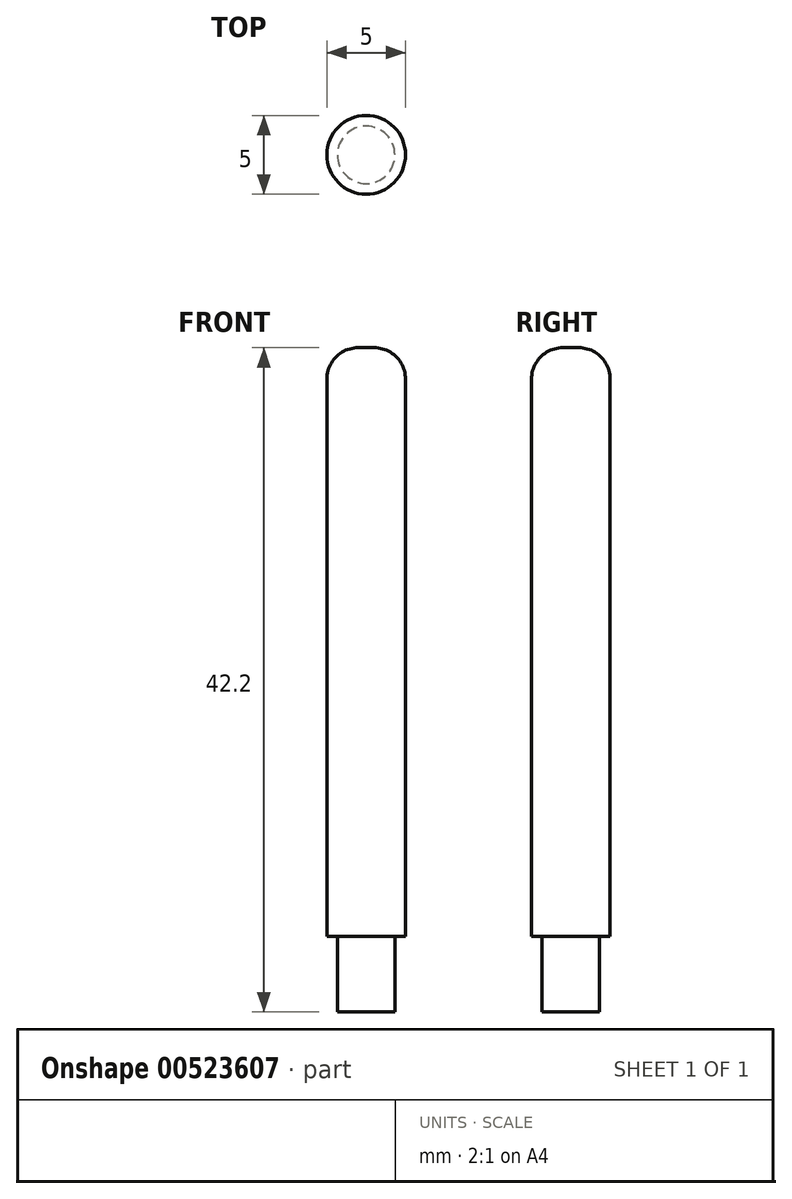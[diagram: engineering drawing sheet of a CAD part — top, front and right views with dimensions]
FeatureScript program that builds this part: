
annotation { "Feature Type Name" : "Feature", "Feature Type Description" : "" }
export const myFeature = defineFeature(function(context is Context, id is Id, definition is map)
    precondition{}
    {
        {
            var Q0;
            Q0=qCreatedBy(makeId("Top.planeOp"),FACE);
            var sketch = newSketch(context, id + "F0", { "sketchPlane" : qUnion([Q0])});
            skCircle(sketch, "E0", {"center": v(0, 0) * mm, "radius": 2.5 * mm});
            skSolve(sketch);
        }
        {
            var Q0;
            Q0 = qSketchRegion(id + "F0", true);
            extrude(context, id + "F1", {"entities" : qUnion([Q0]), "depth" : 37.4 * mm, "offsetDistance" : 25 * mm});
        }
        {
            var Q0;
            Q0=makeQuery(id+"F1.opExtrude","CAP_EDGE",EDGE,{"disambiguationData":[OSD([sQuery(id+"F0.wireOp",EDGE,"E0")])],"isStart":false});
            fillet(context, id + "F2", {"entities" : qUnion([Q0]), "radius" : 2 * mm, "tangentPropagation" : true, "allowEdgeOverflow" : false});
        }
        {
            var Q0;
            Q0=makeQuery(id+"F1.opExtrude","CAP_FACE",FACE,{"disambiguationData":[OSD([sQuery(id+"F0.wireOp",EDGE,"E0")])],"isStart":true});
            var sketch = newSketch(context, id + "F3", { "sketchPlane" : qUnion([Q0])});
            skCircle(sketch, "E1", {"center": v(0, 0) * mm, "radius": 1.82 * mm});
            skSolve(sketch);
        }
        {
            var Q0;
            Q0=makeQuery(id+"F3.imprint","IMPRINT",FACE,{"disambiguationData":[TD([[makeQuery(id+"F3.imprint","IMPRINT",EDGE,{"derivedFrom":sQuery(id+"F3.wireOp",EDGE,"E1")}),1.0]])]});
            extrude(context, id + "F4", {"entities" : qUnion([Q0]), "operationType" : NewBodyOperationType.ADD, "depth" : 4.8 * mm, "offsetDistance" : 25 * mm});
        }
    });
